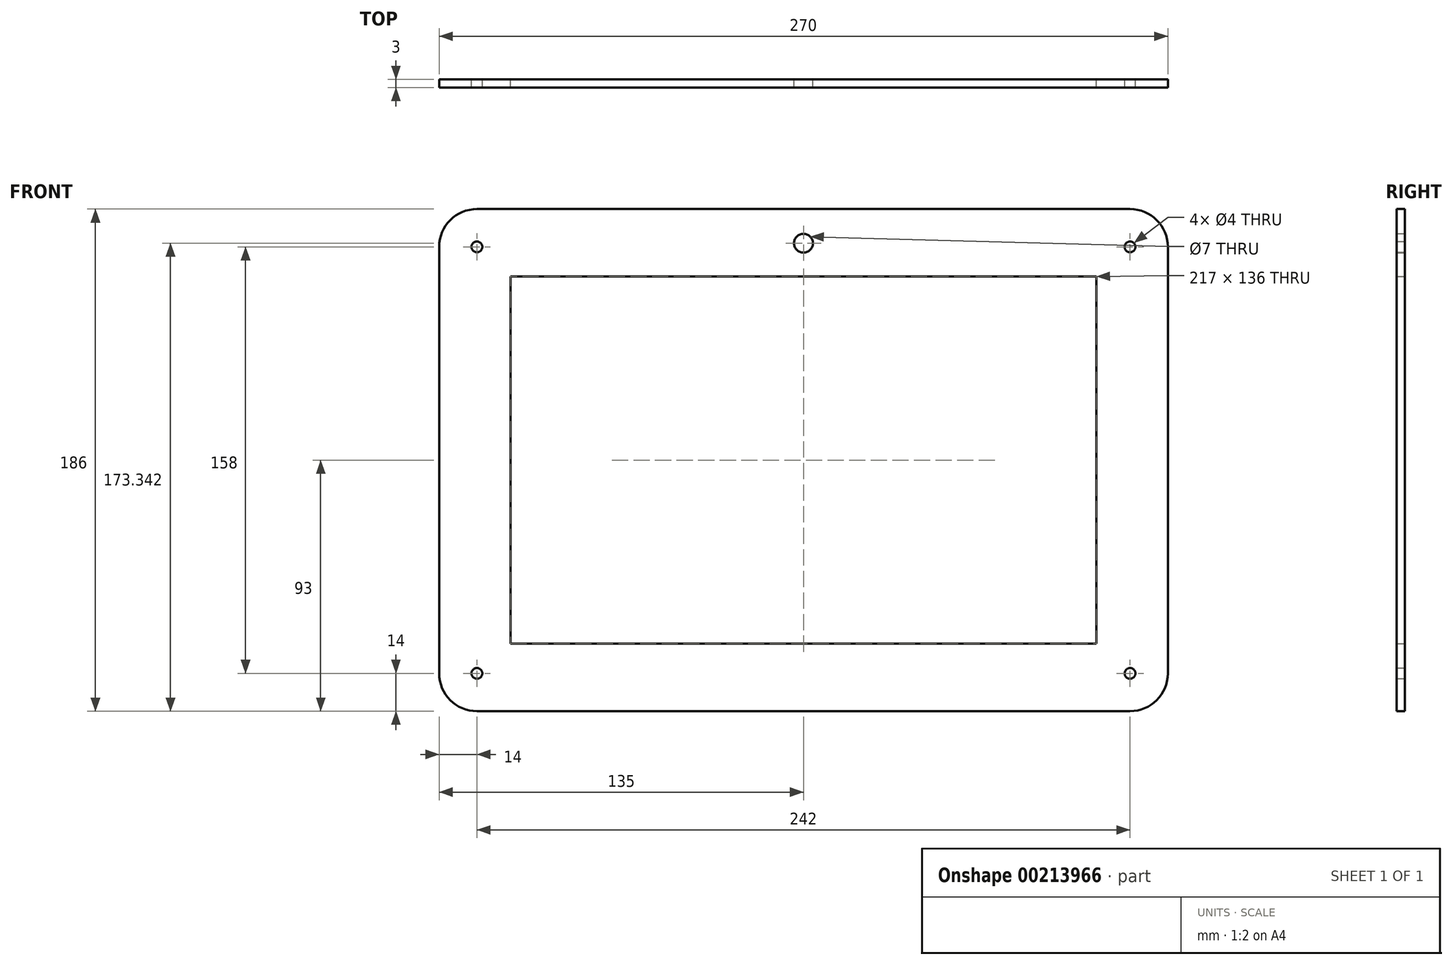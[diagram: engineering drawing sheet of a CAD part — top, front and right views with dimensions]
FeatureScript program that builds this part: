
annotation { "Feature Type Name" : "Feature", "Feature Type Description" : "" }
export const myFeature = defineFeature(function(context is Context, id is Id, definition is map)
    precondition{}
    {
        {
            var Q0;
            Q0=qCreatedBy(makeId("Front.planeOp"),FACE);
            var sketch = newSketch(context, id + "F0", { "sketchPlane" : qUnion([Q0])});
            skLineSegment(sketch, "E0.bottom", {"start": v(121, -93) * mm, "end": v(-121, -93) * mm});
            skLineSegment(sketch, "E0.top", {"start": v(121, 93) * mm, "end": v(-121, 93) * mm});
            skLineSegment(sketch, "E0.left", {"start": v(135, -79) * mm, "end": v(135, 79) * mm});
            skLineSegment(sketch, "E0.right", {"start": v(-135, -79) * mm, "end": v(-135, 79) * mm});
            skPoint(sketch, "E0.middle", {"position": v(0, 0) * mm});
            skPoint(sketch, "E1.visualSharp", {"position": v(-135, 93) * mm});
            skArc(sketch, "E1.filletArc", {"start": v(-121, 93) * mm, "mid": v(-130.9, 88.9) * mm, "end": v(-135, 79) * mm});
            skPoint(sketch, "E2.visualSharp", {"position": v(-135, -93) * mm});
            skArc(sketch, "E2.filletArc", {"start": v(-135, -79) * mm, "mid": v(-130.9, -88.9) * mm, "end": v(-121, -93) * mm});
            skPoint(sketch, "E3.visualSharp", {"position": v(135, -93) * mm});
            skArc(sketch, "E3.filletArc", {"start": v(121, -93) * mm, "mid": v(130.9, -88.9) * mm, "end": v(135, -79) * mm});
            skPoint(sketch, "E4.visualSharp", {"position": v(135, 93) * mm});
            skArc(sketch, "E4.filletArc", {"start": v(135, 79) * mm, "mid": v(130.9, 88.9) * mm, "end": v(121, 93) * mm});
            skLineSegment(sketch, "E5.bottom", {"start": v(108.5, -68) * mm, "end": v(-108.5, -68) * mm});
            skLineSegment(sketch, "E5.top", {"start": v(108.5, 68) * mm, "end": v(-108.5, 68) * mm});
            skLineSegment(sketch, "E5.left", {"start": v(108.5, -68) * mm, "end": v(108.5, 68) * mm});
            skLineSegment(sketch, "E5.right", {"start": v(-108.5, -68) * mm, "end": v(-108.5, 68) * mm});
            skLineSegment(sketch, "E6", {"start": v(0, 0) * mm, "end": v(0, 80.34) * mm});
            skPoint(sketch, "E6.endSnap0", {"position": v(0, 68) * mm});
            skCircle(sketch, "E7", {"center": v(0, 80.34) * mm, "radius": 3.5 * mm});
            skCircle(sketch, "E8", {"center": v(-121, -79) * mm, "radius": 2 * mm});
            skCircle(sketch, "E9", {"center": v(121, -79) * mm, "radius": 2 * mm});
            skCircle(sketch, "E10", {"center": v(-121, 79) * mm, "radius": 2 * mm});
            skCircle(sketch, "E11", {"center": v(121, 79) * mm, "radius": 2 * mm});
            skSolve(sketch);
        }
        {
            var Q0;
            Q0=makeQuery(id+"F0.imprint","IMPRINT",FACE,{"disambiguationData":[TD([[makeQuery(id+"F0.imprint","IMPRINT",EDGE,{"derivedFrom":sQuery(id+"F0.wireOp",EDGE,"E0.bottom")}),-1.0]])]});
            extrude(context, id + "F1", {"entities" : qUnion([Q0]), "depth" : 3 * mm});
        }
    });
